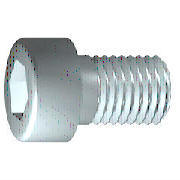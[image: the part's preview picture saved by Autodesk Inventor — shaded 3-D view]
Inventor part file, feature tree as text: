
AUTODESK INVENTOR PART (.ipt)
format: ipt  version: 2022.1 (Build 261234000, 234)  size: 191,488 bytes
history: native  units: mm (DEFAULTED — no unit token found)
features: sketch x2, other x1, extrude x1, plane x1, fillet x1
ambient origin geometry x7: Origin, YZ Plane, XY Plane, X Axis, Y Axis, Z Axis, Center Point
bodies: Solid1 (feature_tree)
feature tree (6):
  other  "Cuerpo"
  extrude  "Ranura"  Depth=3.0mm
  plane  "Work Plane1"
  fillet  "Fillet2"  Radius=3.0mm
  sketch  "Boceto1"  dims[d1=14.75mm d2=0.306825mm d3=3.0mm]
  sketch  "Boceto2"  dims[d4=1.3mm d5=60.0deg d6=3.0mm d7=3.0mm d8=2.886751mm d9=5.5mm d10=90.0deg d11=10.0mm d12=0.0mm d13=14.75mm d14=0.0mm d15=0.306725mm d16=0.306725mm d17=0.3mm d19=0.0mm d26=16.0mm d27=45.0deg d28=0.0mm d29=0.0mm d30=0.1mm]
